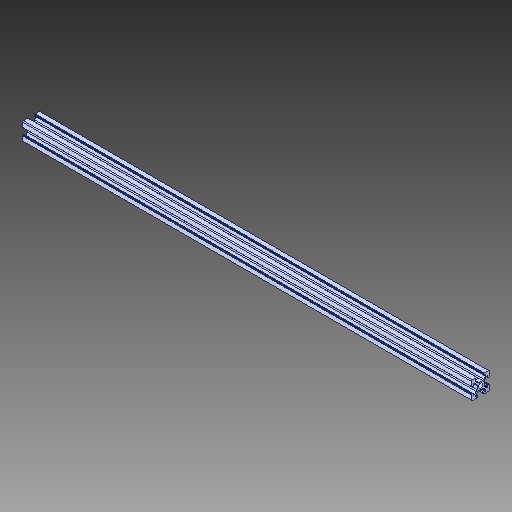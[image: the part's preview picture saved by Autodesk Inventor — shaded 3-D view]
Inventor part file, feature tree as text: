
AUTODESK INVENTOR PART (.ipt)
format: ipt  version: 2018 (Build 220112000, 112)  size: 362,496 bytes
history: native  units: in
note: dims shown in document units (in); Inventor stores cm internally (conversion verified against a paired STEP export)
features: extrude x1, sketch x1, projected_geometry x1, fillet x1
ambient origin geometry x8: Origin, YZ Plane, XZ Plane, XY Plane, X Axis, Y Axis, Z Axis, Center Point
bodies: Solid1 (feature_tree)
feature tree (4):
  extrude  "Extrusion2"  [1 undecoded]
  sketch  "Sketch3"  dims[d2=15.748in d3=0.0in]
  projected_geometry  "Projected Loop2"
  fillet  "Fillet5"  [1 undecoded]
note: 2 required parameter values undecoded (feature->parameter linkage not recoverable at this tier; creation-order binding heuristic only, values carry confidence <= 0.55)
